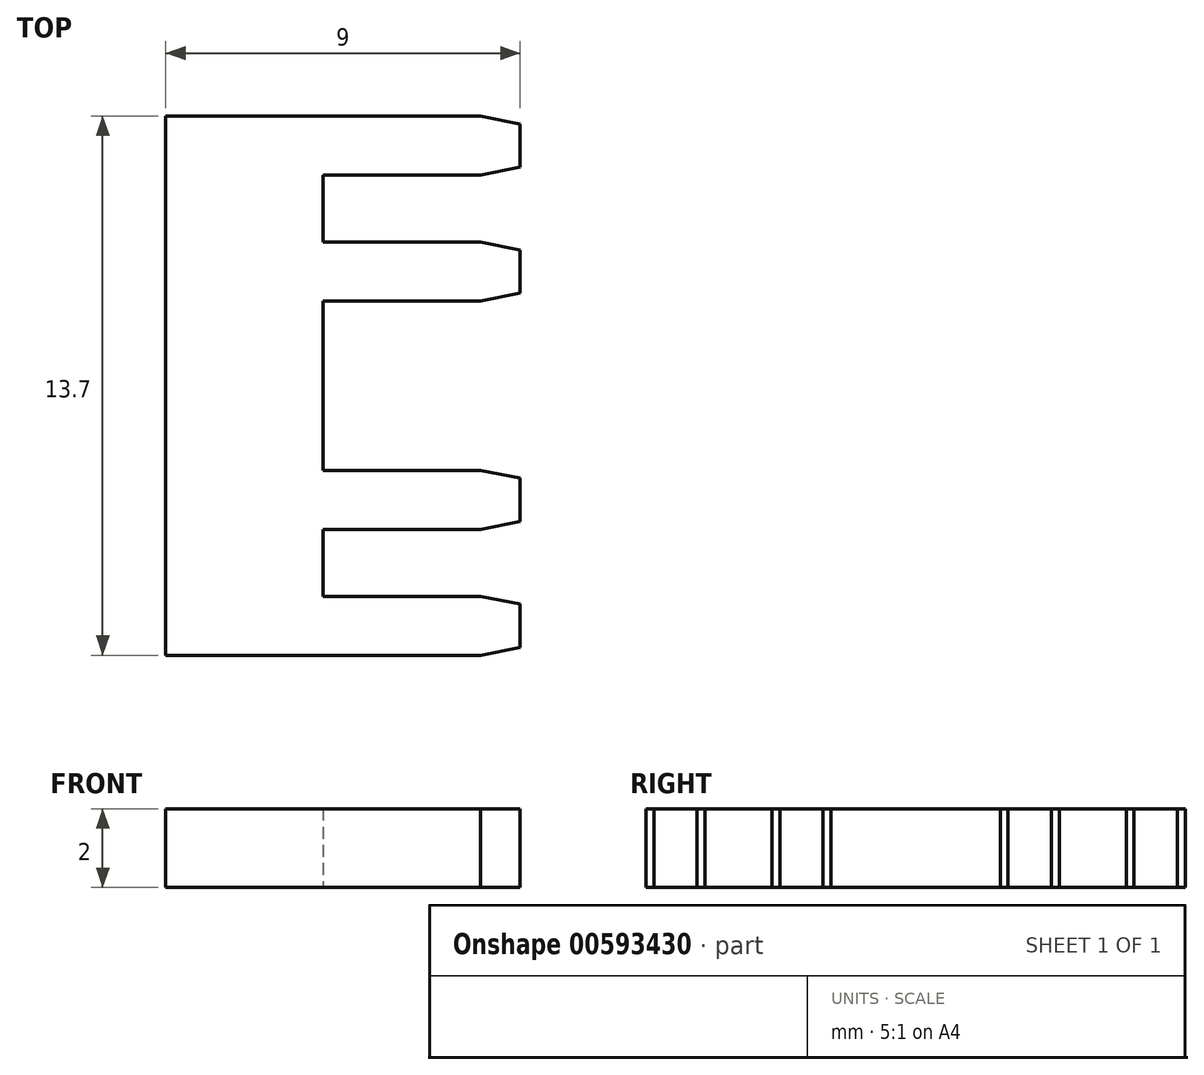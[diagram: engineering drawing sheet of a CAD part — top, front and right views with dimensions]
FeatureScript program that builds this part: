
annotation { "Feature Type Name" : "Feature", "Feature Type Description" : "" }
export const myFeature = defineFeature(function(context is Context, id is Id, definition is map)
    precondition{}
    {
        {
            var Q0;
            Q0=qCreatedBy(makeId("Top.planeOp"),FACE);
            var sketch = newSketch(context, id + "F0", { "sketchPlane" : qUnion([Q0])});
            skLineSegment(sketch, "E0", {"start": v(0, 0) * mm, "end": v(9, 0) * mm});
            skLineSegment(sketch, "E1", {"start": v(9, 0) * mm, "end": v(9, 1.5) * mm});
            skLineSegment(sketch, "E2", {"start": v(9, 1.5) * mm, "end": v(4, 1.5) * mm});
            skLineSegment(sketch, "E3", {"start": v(4, 1.5) * mm, "end": v(4, 3.2) * mm});
            skLineSegment(sketch, "E4", {"start": v(4, 3.2) * mm, "end": v(9, 3.2) * mm});
            skLineSegment(sketch, "E5", {"start": v(9, 3.2) * mm, "end": v(9, 4.7) * mm});
            skLineSegment(sketch, "E6", {"start": v(9, 4.7) * mm, "end": v(4, 4.7) * mm});
            skLineSegment(sketch, "E7", {"start": v(4, 4.7) * mm, "end": v(4, 9) * mm});
            skLineSegment(sketch, "E8", {"start": v(4, 9) * mm, "end": v(9, 9) * mm});
            skLineSegment(sketch, "E9", {"start": v(9, 9) * mm, "end": v(9, 10.5) * mm});
            skLineSegment(sketch, "E10", {"start": v(9, 10.5) * mm, "end": v(4, 10.5) * mm});
            skLineSegment(sketch, "E11", {"start": v(4, 10.5) * mm, "end": v(4, 12.2) * mm});
            skLineSegment(sketch, "E12", {"start": v(4, 12.2) * mm, "end": v(9, 12.2) * mm});
            skLineSegment(sketch, "E13", {"start": v(9, 12.2) * mm, "end": v(9, 13.7) * mm});
            skLineSegment(sketch, "E14", {"start": v(9, 13.7) * mm, "end": v(4, 13.7) * mm});
            skLineSegment(sketch, "E15", {"start": v(4, 13.7) * mm, "end": v(0, 13.7) * mm});
            skLineSegment(sketch, "E16", {"start": v(0, 13.7) * mm, "end": v(0, 0) * mm});
            skSolve(sketch);
        }
        {
            var Q0;
            Q0 = qSketchRegion(id + "F0", true);
            extrude(context, id + "F1", {"entities" : qUnion([Q0]), "depth" : 2 * mm, "offsetDistance" : 25 * mm});
        }
        {
            var Q0;
            Q0=makeQuery(id+"F1.opExtrude","SWEPT_EDGE",EDGE,{"disambiguationData":[OSD([sQuery(id+"F0.wireOp",EDGE,"E12"),sQuery(id+"F0.wireOp",EDGE,"E13")])]});
            var Q1;
            Q1=makeQuery(id+"F1.opExtrude","SWEPT_EDGE",EDGE,{"disambiguationData":[OSD([sQuery(id+"F0.wireOp",EDGE,"E8"),sQuery(id+"F0.wireOp",EDGE,"E9")])]});
            var Q2;
            Q2=makeQuery(id+"F1.opExtrude","SWEPT_EDGE",EDGE,{"disambiguationData":[OSD([sQuery(id+"F0.wireOp",EDGE,"E4"),sQuery(id+"F0.wireOp",EDGE,"E5")])]});
            var Q3;
            Q3=makeQuery(id+"F1.opExtrude","SWEPT_EDGE",EDGE,{"disambiguationData":[OSD([sQuery(id+"F0.wireOp",EDGE,"E0"),sQuery(id+"F0.wireOp",EDGE,"E1")])]});
            chamfer(context, id + "F2", {"entities" : qUnion([Q0, Q1, Q2, Q3]), "chamferType" : ChamferType.TWO_OFFSETS, "width1" : .2 * mm, "oppositeDirection" : false, "width2" : 1 * mm, "tangentPropagation" : true});
        }
        {
            var Q0;
            Q0=makeQuery(id+"F1.opExtrude","SWEPT_EDGE",EDGE,{"disambiguationData":[OSD([sQuery(id+"F0.wireOp",EDGE,"E9"),sQuery(id+"F0.wireOp",EDGE,"E10")])]});
            var Q1;
            Q1=makeQuery(id+"F1.opExtrude","SWEPT_EDGE",EDGE,{"disambiguationData":[OSD([sQuery(id+"F0.wireOp",EDGE,"E5"),sQuery(id+"F0.wireOp",EDGE,"E6")])]});
            var Q2;
            Q2=makeQuery(id+"F1.opExtrude","SWEPT_EDGE",EDGE,{"disambiguationData":[OSD([sQuery(id+"F0.wireOp",EDGE,"E1"),sQuery(id+"F0.wireOp",EDGE,"E2")])]});
            var Q3;
            Q3=makeQuery(id+"F1.opExtrude","SWEPT_EDGE",EDGE,{"disambiguationData":[OSD([sQuery(id+"F0.wireOp",EDGE,"E13"),sQuery(id+"F0.wireOp",EDGE,"E14")])]});
            chamfer(context, id + "F3", {"entities" : qUnion([Q0, Q1, Q2, Q3]), "chamferType" : ChamferType.TWO_OFFSETS, "width1" : 1 * mm, "oppositeDirection" : false, "width2" : .2 * mm, "tangentPropagation" : true});
        }
    });
